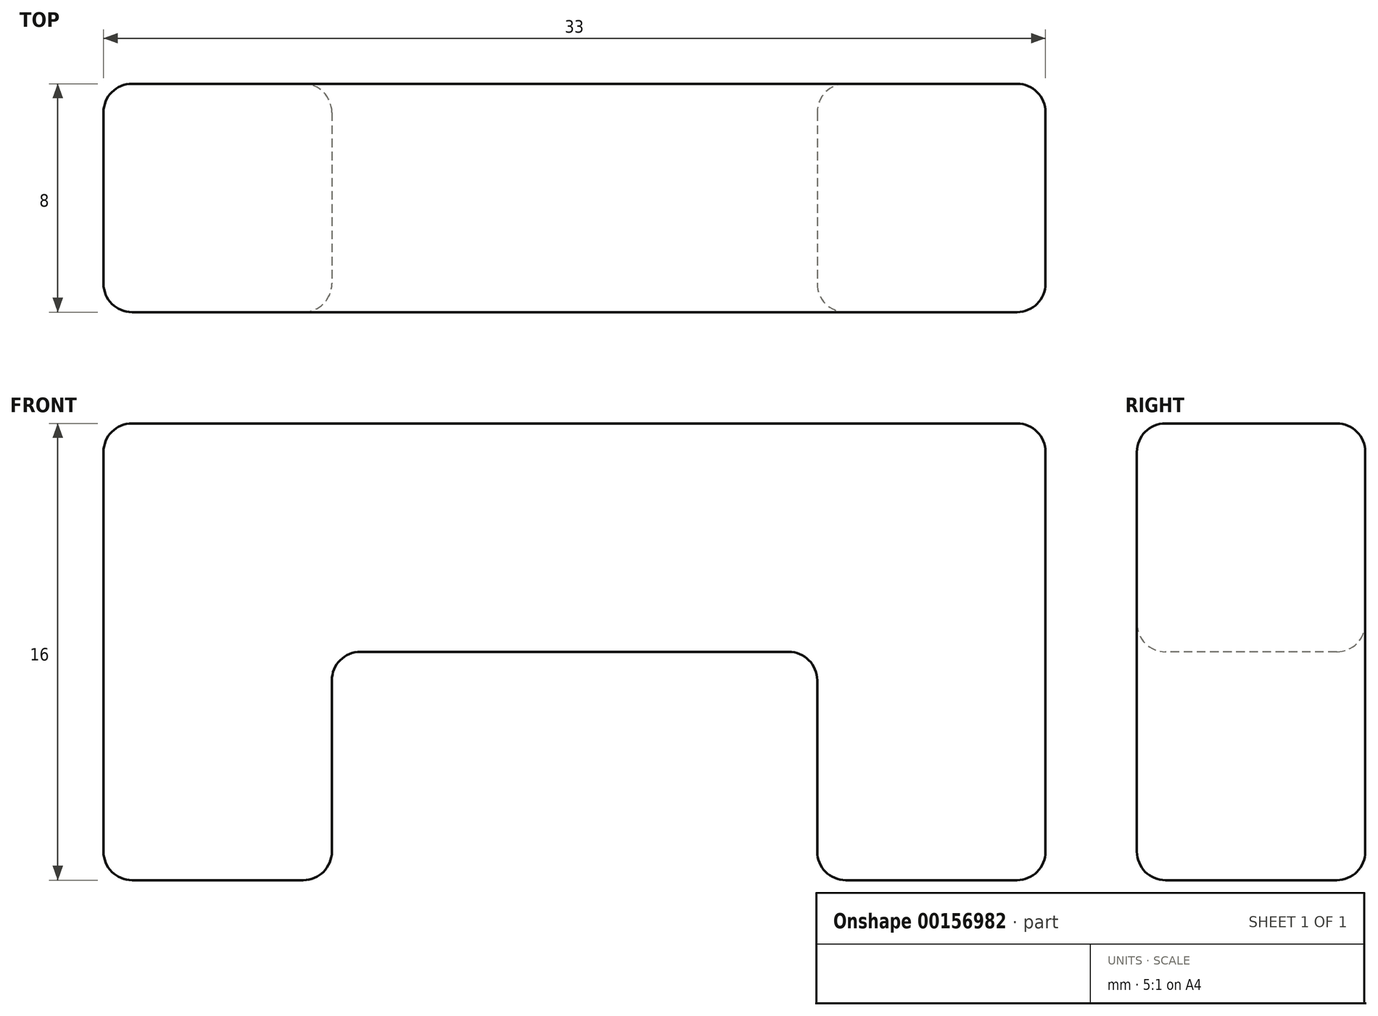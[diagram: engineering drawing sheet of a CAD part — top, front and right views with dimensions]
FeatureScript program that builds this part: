
annotation { "Feature Type Name" : "Feature", "Feature Type Description" : "" }
export const myFeature = defineFeature(function(context is Context, id is Id, definition is map)
    precondition{}
    {
        {
            var Q0;
            Q0=qCreatedBy(makeId("Front.planeOp"),FACE);
            var sketch = newSketch(context, id + "F0", { "sketchPlane" : qUnion([Q0])});
            skLineSegment(sketch, "E0.bottom", {"start": v(-16.5, 8) * mm, "end": v(16.5, 8) * mm});
            skLineSegment(sketch, "E0.top", {"start": v(-16.5, -8) * mm, "end": v(16.5, -8) * mm});
            skLineSegment(sketch, "E0.left", {"start": v(-16.5, 8) * mm, "end": v(-16.5, -8) * mm});
            skLineSegment(sketch, "E0.right", {"start": v(16.5, 8) * mm, "end": v(16.5, -8) * mm});
            skLineSegment(sketch, "E1", {"start": v(0, 8) * mm, "end": v(0, 0) * mm, "construction": true});
            skSolve(sketch);
        }
        {
            var Q0;
            Q0=makeQuery(id+"F0.imprint","IMPRINT",FACE,{"disambiguationData":[TD([[makeQuery(id+"F0.imprint","IMPRINT",EDGE,{"derivedFrom":sQuery(id+"F0.wireOp",EDGE,"E0.bottom")}),-1.0]])]});
            extrude(context, id + "F1", {"entities" : qUnion([Q0]), "depth" : 8 * mm});
        }
        {
            var Q0;
            Q0=makeQuery(id+"F1.opExtrude","CAP_FACE",FACE,{"disambiguationData":[OSD([sQuery(id+"F0.wireOp",EDGE,"E0.bottom"),sQuery(id+"F0.wireOp",EDGE,"E0.top"),sQuery(id+"F0.wireOp",EDGE,"E0.left"),sQuery(id+"F0.wireOp",EDGE,"E0.right")])],"isStart":false});
            var sketch = newSketch(context, id + "F2", { "sketchPlane" : qUnion([Q0])});
            skLineSegment(sketch, "E2.bottom", {"start": v(-8.5, 0) * mm, "end": v(8.5, 0) * mm});
            skLineSegment(sketch, "E2.top", {"start": v(-8.5, -8) * mm, "end": v(8.5, -8) * mm});
            skLineSegment(sketch, "E2.left", {"start": v(-8.5, 0) * mm, "end": v(-8.5, -8) * mm});
            skLineSegment(sketch, "E2.right", {"start": v(8.5, 0) * mm, "end": v(8.5, -8) * mm});
            skSolve(sketch);
        }
        {
            var Q0;
            Q0 = qSketchRegion(id + "F2", true);
            extrude(context, id + "F3", {"entities" : qUnion([Q0]), "operationType" : NewBodyOperationType.REMOVE, "oppositeDirection" : true, "depth" : 25 * mm});
        }
        {
            var Q0;
            Q0=makeQuery(id+"F1.opExtrude","CAP_FACE",FACE,{"disambiguationData":[OSD([sQuery(id+"F0.wireOp",EDGE,"E0.bottom"),sQuery(id+"F0.wireOp",EDGE,"E0.top"),sQuery(id+"F0.wireOp",EDGE,"E0.left"),sQuery(id+"F0.wireOp",EDGE,"E0.right")])],"isStart":false});
            var Q1;
            Q1=makeQuery(id+"F3.boolean.opBoolean","INTERSECT",EDGE,{"derivedFrom":[makeQuery(id+"F1.opExtrude","CAP_FACE",FACE,{"disambiguationData":[OSD([sQuery(id+"F0.wireOp",EDGE,"E0.bottom"),sQuery(id+"F0.wireOp",EDGE,"E0.top"),sQuery(id+"F0.wireOp",EDGE,"E0.left"),sQuery(id+"F0.wireOp",EDGE,"E0.right")])],"isStart":true}),makeQuery(id+"F3.opExtrude","SWEPT_FACE",FACE,{"disambiguationData":[OSD([sQuery(id+"F2.wireOp",EDGE,"E2.left")])]})]});
            var Q2;
            Q2=makeQuery(id+"F1.opExtrude","CAP_FACE",FACE,{"disambiguationData":[OSD([sQuery(id+"F0.wireOp",EDGE,"E0.bottom"),sQuery(id+"F0.wireOp",EDGE,"E0.top"),sQuery(id+"F0.wireOp",EDGE,"E0.left"),sQuery(id+"F0.wireOp",EDGE,"E0.right")])],"isStart":true});
            var Q3;
            Q3=makeQuery(id+"F3.boolean.opBoolean","COPY",FACE,{"derivedFrom":makeQuery(id+"F3.opExtrude","SWEPT_FACE",FACE,{"disambiguationData":[OSD([sQuery(id+"F2.wireOp",EDGE,"E2.bottom")])]})});
            var Q4;
            {var subQ1=sQuery(id+"F0.wireOp",EDGE,"E0.left");var subQ2=sQuery(id+"F0.wireOp",EDGE,"E0.top");Q4=makeQuery(id+"F3.boolean.opBoolean","SPLIT",FACE,{"disambiguationData":[TD([makeQuery(id+"F1.opExtrude","SWEPT_FACE",FACE,{"disambiguationData":[OSD([subQ1])]})])],"derivedFrom":makeQuery(id+"F1.opExtrude","SWEPT_FACE",FACE,{"disambiguationData":[OSD([subQ2])]})});}
            var Q5;
            {var subQ0=sQuery(id+"F0.wireOp",EDGE,"E0.right");var subQ2=sQuery(id+"F0.wireOp",EDGE,"E0.top");Q5=makeQuery(id+"F3.boolean.opBoolean","SPLIT",FACE,{"disambiguationData":[TD([makeQuery(id+"F1.opExtrude","SWEPT_FACE",FACE,{"disambiguationData":[OSD([subQ0])]})])],"derivedFrom":makeQuery(id+"F1.opExtrude","SWEPT_FACE",FACE,{"disambiguationData":[OSD([subQ2])]})});}
            var Q6;
            Q6=makeQuery(id+"F1.opExtrude","SWEPT_FACE",FACE,{"disambiguationData":[OSD([sQuery(id+"F0.wireOp",EDGE,"E0.bottom")])]});
            fillet(context, id + "F4", {"entities" : qUnion([Q0, Q1, Q2, Q3, Q4, Q5, Q6]), "radius" : 1 * mm, "tangentPropagation" : true, "allowEdgeOverflow" : false});
        }
    });
